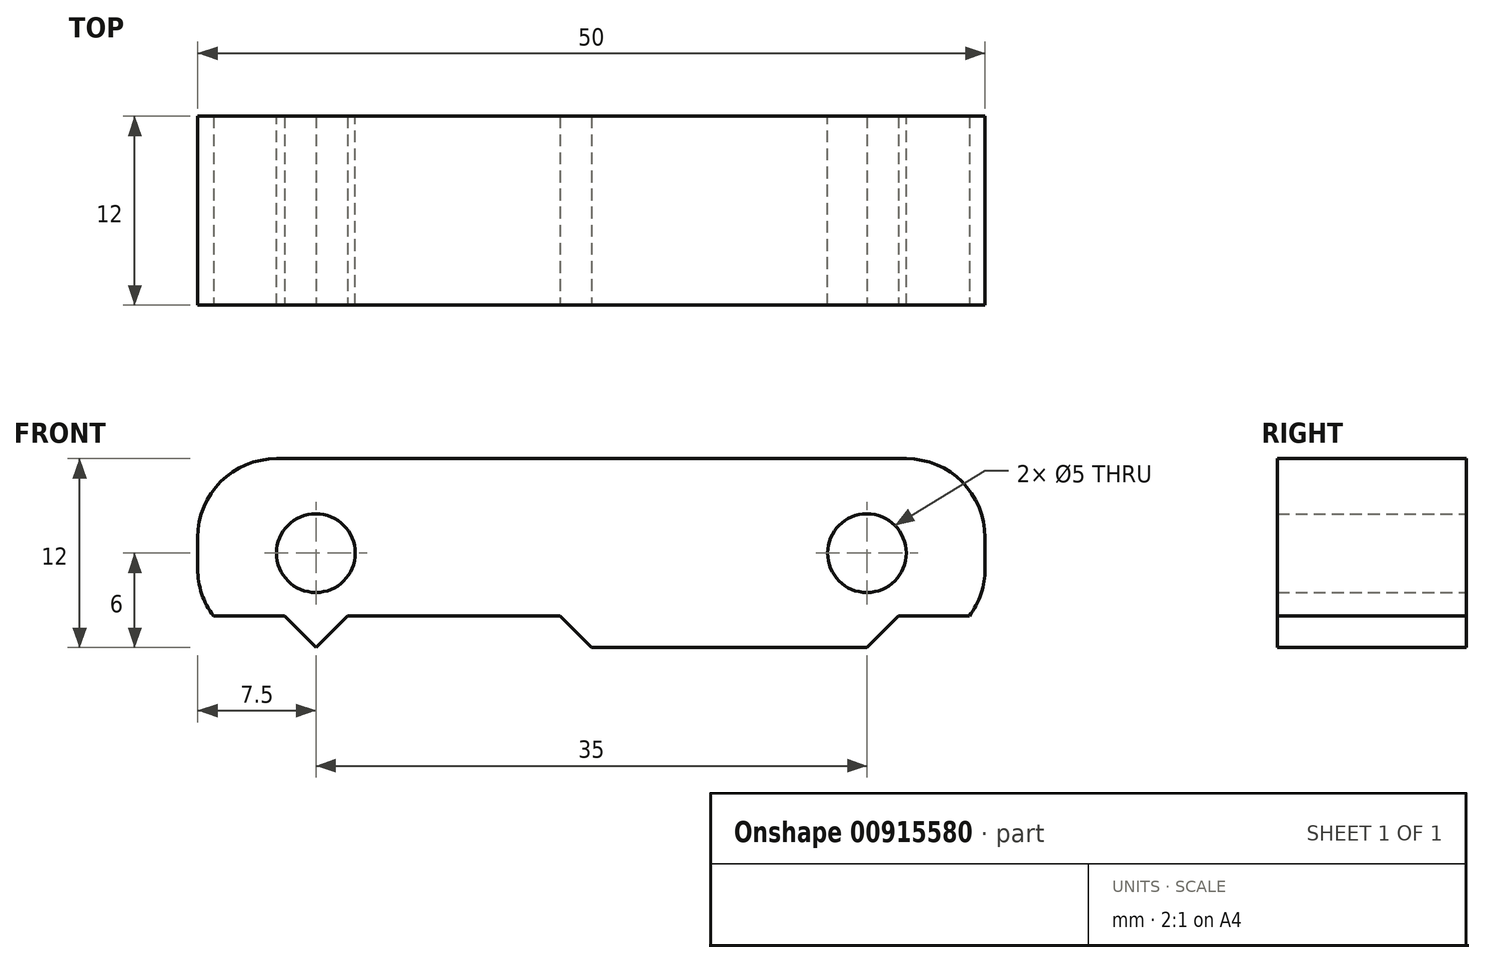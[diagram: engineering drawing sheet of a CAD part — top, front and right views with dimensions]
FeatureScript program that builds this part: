
annotation { "Feature Type Name" : "Feature", "Feature Type Description" : "" }
export const myFeature = defineFeature(function(context is Context, id is Id, definition is map)
    precondition{}
    {
        {
            var Q0;
            Q0=qCreatedBy(makeId("Front.planeOp"),FACE);
            var sketch = newSketch(context, id + "F0", { "sketchPlane" : qUnion([Q0])});
            skLineSegment(sketch, "E0.bottom", {"start": v(25, 6) * mm, "end": v(-25, 6) * mm});
            skLineSegment(sketch, "E0.top", {"start": v(25, -6) * mm, "end": v(-25, -6) * mm});
            skLineSegment(sketch, "E0.left", {"start": v(25, 6) * mm, "end": v(25, -6) * mm});
            skLineSegment(sketch, "E0.right", {"start": v(-25, 6) * mm, "end": v(-25, -6) * mm});
            skPoint(sketch, "E0.middle", {"position": v(0, 0) * mm});
            skCircle(sketch, "E1", {"center": v(-17.5, 0) * mm, "radius": 2.5 * mm});
            skCircle(sketch, "E2", {"center": v(17.5, 0) * mm, "radius": 2.5 * mm});
            skPoint(sketch, "E3.orphan", {"position": v(17.5, -2.07) * mm});
            skPoint(sketch, "E4.left.start.orphan", {"position": v(17.5, 2.07) * mm});
            skPoint(sketch, "E5.orphan", {"position": v(-17.5, 2.07) * mm});
            skPoint(sketch, "E4.right.end.orphan", {"position": v(-17.5, -2.07) * mm});
            skSolve(sketch);
        }
        {
            var Q0;
            Q0=makeQuery(id+"F0.imprint","IMPRINT",FACE,{"disambiguationData":[TD([[makeQuery(id+"F0.imprint","IMPRINT",EDGE,{"derivedFrom":sQuery(id+"F0.wireOp",EDGE,"E0.bottom")}),1.0]])]});
            extrude(context, id + "F1", {"entities" : qUnion([Q0]), "depth" : 12 * mm, "offsetDistance" : 25 * mm});
        }
        {
            var Q0;
            Q0=makeQuery(id+"F1.opExtrude","SWEPT_EDGE",EDGE,{"disambiguationData":[OSD([sQuery(id+"F0.wireOp",EDGE,"E0.bottom"),sQuery(id+"F0.wireOp",EDGE,"E0.right")])]});
            var Q1;
            Q1=makeQuery(id+"F1.opExtrude","SWEPT_EDGE",EDGE,{"disambiguationData":[OSD([sQuery(id+"F0.wireOp",EDGE,"E0.bottom"),sQuery(id+"F0.wireOp",EDGE,"E0.left")])]});
            var Q2;
            Q2=makeQuery(id+"F1.opExtrude","SWEPT_EDGE",EDGE,{"disambiguationData":[OSD([sQuery(id+"F0.wireOp",EDGE,"E0.top"),sQuery(id+"F0.wireOp",EDGE,"E0.left")])]});
            var Q3;
            Q3=makeQuery(id+"F1.opExtrude","SWEPT_EDGE",EDGE,{"disambiguationData":[OSD([sQuery(id+"F0.wireOp",EDGE,"E0.top"),sQuery(id+"F0.wireOp",EDGE,"E0.right")])]});
            fillet(context, id + "F2", {"entities" : qUnion([Q0, Q1, Q2, Q3]), "radius" : 5 * mm, "tangentPropagation" : true, "allowEdgeOverflow" : false});
        }
        {
            var Q0;
            Q0=makeQuery(id+"F1.opExtrude","CAP_FACE",FACE,{"disambiguationData":[OSD([sQuery(id+"F0.wireOp",EDGE,"E0.bottom"),sQuery(id+"F0.wireOp",EDGE,"E0.top"),sQuery(id+"F0.wireOp",EDGE,"E0.left"),sQuery(id+"F0.wireOp",EDGE,"E0.right"),sQuery(id+"F0.wireOp",EDGE,"E1"),sQuery(id+"F0.wireOp",EDGE,"E2")])],"isStart":false});
            var sketch = newSketch(context, id + "F3", { "sketchPlane" : qUnion([Q0])});
            skLineSegment(sketch, "E6", {"start": v(0, -6) * mm, "end": v(2, -4) * mm});
            skLineSegment(sketch, "E7", {"start": v(2, -4) * mm, "end": v(0, -6) * mm});
            skLineSegment(sketch, "E8", {"start": v(0, -6) * mm, "end": v(-2, -4) * mm});
            skLineSegment(sketch, "E9", {"start": v(2, -4) * mm, "end": v(15.5, -4) * mm});
            skLineSegment(sketch, "E10", {"start": v(15.5, -4) * mm, "end": v(17.5, -6) * mm});
            skLineSegment(sketch, "E11", {"start": v(18.65, -4) * mm, "end": v(24, -4) * mm});
            skLineSegment(sketch, "E12", {"start": v(24, -4) * mm, "end": v(25, -8) * mm});
            skLineSegment(sketch, "E13", {"start": v(25, -8) * mm, "end": v(8.25, -12.19) * mm});
            skLineSegment(sketch, "E14", {"start": v(8.25, -12.19) * mm, "end": v(-22.98, -10.91) * mm});
            skLineSegment(sketch, "E15", {"start": v(-22.98, -10.91) * mm, "end": v(-26.03, -4) * mm});
            skLineSegment(sketch, "E16", {"start": v(-26.03, -4) * mm, "end": v(-19.5, -4) * mm});
            skLineSegment(sketch, "E17", {"start": v(-19.5, -4) * mm, "end": v(-17.5, -6) * mm});
            skLineSegment(sketch, "E18", {"start": v(-17.5, -6) * mm, "end": v(-15.5, -4) * mm});
            skLineSegment(sketch, "E19", {"start": v(-15.5, -4) * mm, "end": v(-2, -4) * mm});
            skLineSegment(sketch, "E20", {"start": v(17.5, 0) * mm, "end": v(17.5, -6) * mm});
            skPoint(sketch, "E20.endSnap0", {"position": v(24.5, -6) * mm});
            skLineSegment(sketch, "E21", {"start": v(-17.5, 0) * mm, "end": v(-17.5, -6) * mm});
            skLineSegment(sketch, "E22", {"start": v(17.5, -6) * mm, "end": v(19.5, -4) * mm});
            skSolve(sketch);
        }
        {
            var Q0;
            {var subQ0=sQuery(id+"F3.wireOp",EDGE,"E7");Q0=makeQuery(id+"F3.imprint","IMPRINT",FACE,{"disambiguationData":[TD([[makeQuery(id+"F3.imprint","IMPRINT",EDGE,{"derivedFrom":subQ0}),1.0]])]});}
            var Q1;
            {var subQ0=sQuery(id+"F3.wireOp",EDGE,"E8");Q1=makeQuery(id+"F3.imprint","IMPRINT",FACE,{"disambiguationData":[TD([[makeQuery(id+"F3.imprint","IMPRINT",EDGE,{"derivedFrom":subQ0}),1.0]])]});}
            var Q2;
            {var subQ5=sQuery(id+"F3.wireOp",EDGE,"E22");Q2=makeQuery(id+"F3.imprint","IMPRINT",FACE,{"disambiguationData":[TD([[makeQuery(id+"F3.imprint","IMPRINT",EDGE,{"derivedFrom":subQ5}),-1.0]])]});}
            var Q3;
            {var subQ0=sQuery(id+"F3.wireOp",EDGE,"E17");Q3=makeQuery(id+"F3.imprint","IMPRINT",FACE,{"disambiguationData":[TD([[makeQuery(id+"F3.imprint","IMPRINT",EDGE,{"derivedFrom":subQ0}),-1.0]])]});}
            extrude(context, id + "F4", {"entities" : qUnion([Q0, Q1, Q2, Q3]), "operationType" : NewBodyOperationType.REMOVE, "oppositeDirection" : true, "depth" : 25 * mm, "offsetDistance" : 25 * mm});
        }
    });
